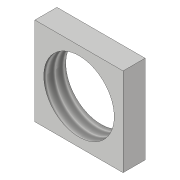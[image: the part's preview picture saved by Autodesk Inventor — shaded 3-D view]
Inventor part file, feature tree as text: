
AUTODESK INVENTOR PART (.ipt)
format: ipt  version: 2019 (Build 230136000, 136)  size: 92,672 bytes
history: native  units: in
note: dims shown in document units (in); Inventor stores cm internally (conversion verified against a paired STEP export)
features: extrude x2, sketch x2, thread x1
ambient origin geometry x8: Origin, YZ Plane, XZ Plane, XY Plane, X Axis, Y Axis, Z Axis, Center Point
bodies: Solid1 (feature_tree)
feature tree (5):
  extrude  "Extrusion1"  Depth=0.7874in
  extrude  "Extrusion2"  Depth=0.3937in
  thread  "Thread1"  [1 undecoded]
  sketch  "Sketch1"  dims[d0=0.7874in d1=0.7874in]
  sketch  "Sketch2"  dims[d2=0.1969in d3=0.0in d4=0.3937in d5=0.3937in d6=0.6299in d7=0.0in d8=0.0in d9=0.3937in d10=0.0in]
note: 1 required parameter value undecoded (feature->parameter linkage not recoverable at this tier; creation-order binding heuristic only, values carry confidence <= 0.55)
